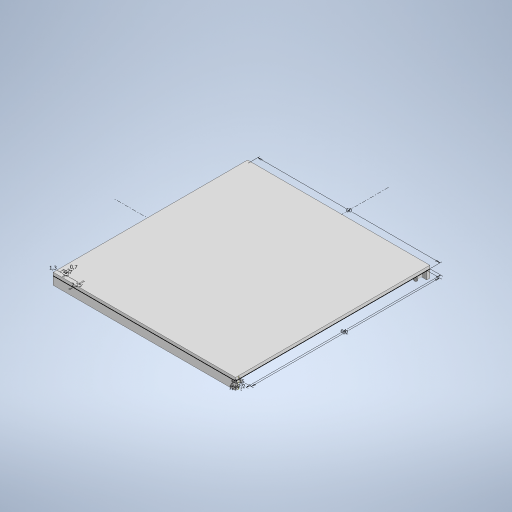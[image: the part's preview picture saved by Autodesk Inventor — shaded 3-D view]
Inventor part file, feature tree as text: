
AUTODESK INVENTOR PART (.ipt)
format: ipt  version: 2023 (Build 270158000, 158)  size: 275,456 bytes
history: native  units: mm
features: extrude x6, sketch x3
ambient origin geometry x8: Origin, YZ Plane, XZ Plane, XY Plane, X Axis, Y Axis, Z Axis, Center Point
bodies: Solido1 (feature_tree)
feature tree (9):
  sketch  "Schizzo1"
  extrude  "Estrusione1"  Depth=60.0mm
  extrude  "Estrusione2"  Depth=64.0mm
  sketch  "Schizzo2"
  extrude  "Estrusione3"  Depth=2.25mm
  extrude  "Estrusione4"  Depth=1.2mm
  sketch  "Schizzo3"
  extrude  "Estrusione5"  Depth=0.7mm
  extrude  "Estrusione6"  Depth=0.7mm
